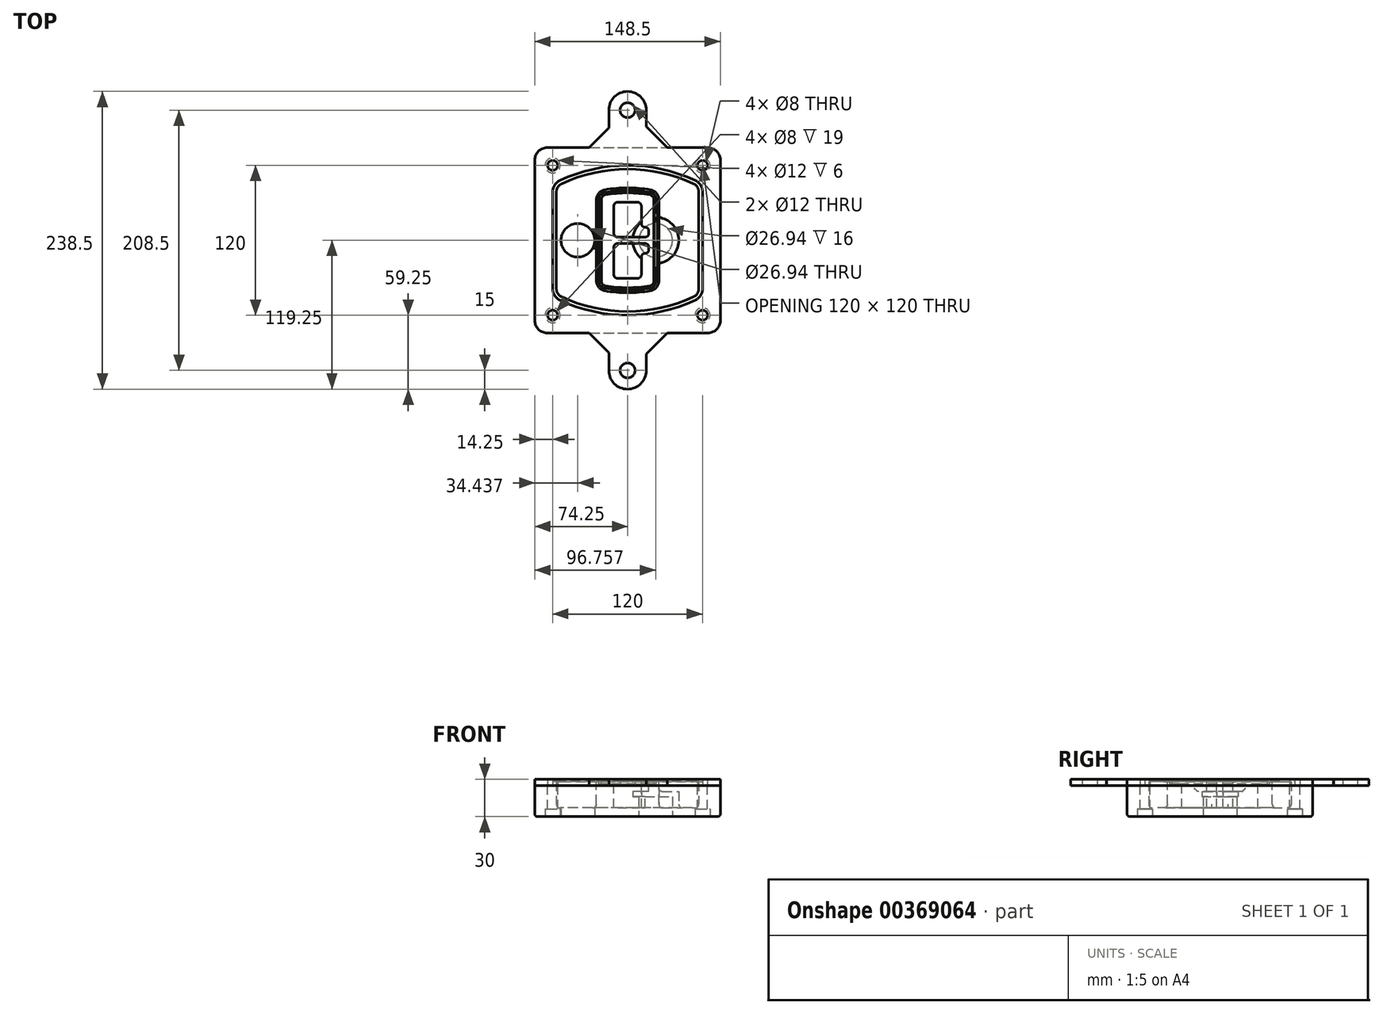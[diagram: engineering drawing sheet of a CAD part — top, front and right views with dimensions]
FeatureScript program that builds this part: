
annotation { "Feature Type Name" : "Feature", "Feature Type Description" : "" }
export const myFeature = defineFeature(function(context is Context, id is Id, definition is map)
    precondition{}
    {
        {
            var Q0;
            Q0=qCreatedBy(makeId("Top.planeOp"),FACE);
            var sketch = newSketch(context, id + "F0", { "sketchPlane" : qUnion([Q0])});
            skPoint(sketch, "E0.rect.middle", {"position": v(0, 0) * mm});
            skLineSegment(sketch, "E1.bottom", {"start": v(-64.25, -74.25) * mm, "end": v(64.25, -74.25) * mm});
            skLineSegment(sketch, "E1.top", {"start": v(-64.25, 74.25) * mm, "end": v(64.25, 74.25) * mm});
            skLineSegment(sketch, "E1.left", {"start": v(-74.25, -64.25) * mm, "end": v(-74.25, 64.25) * mm});
            skLineSegment(sketch, "E1.right", {"start": v(74.25, -64.25) * mm, "end": v(74.25, 64.25) * mm});
            skLineSegment(sketch, "E2", {"start": v(-74.25, 74.25) * mm, "end": v(74.25, -74.25) * mm, "construction": true});
            skLineSegment(sketch, "E3", {"start": v(74.25, 74.25) * mm, "end": v(-74.25, -74.25) * mm, "construction": true});
            skCircle(sketch, "E4", {"center": v(-60, 60) * mm, "radius": 4 * mm});
            skCircle(sketch, "E5", {"center": v(60, 60) * mm, "radius": 4 * mm});
            skCircle(sketch, "E6", {"center": v(60, -60) * mm, "radius": 4 * mm});
            skCircle(sketch, "E7", {"center": v(-60, -60) * mm, "radius": 4 * mm});
            skLineSegment(sketch, "E8", {"start": v(-60, 60) * mm, "end": v(60, 60) * mm, "construction": true});
            skLineSegment(sketch, "E9", {"start": v(60, 60) * mm, "end": v(60, -60) * mm, "construction": true});
            skLineSegment(sketch, "E10", {"start": v(60, -60) * mm, "end": v(-60, -60) * mm, "construction": true});
            skLineSegment(sketch, "E11", {"start": v(-60, -60) * mm, "end": v(-60, 60) * mm, "construction": true});
            skLineSegment(sketch, "E12", {"start": v(-60, 38.83) * mm, "end": v(-60, -38.83) * mm});
            skLineSegment(sketch, "E13", {"start": v(60, 38.83) * mm, "end": v(60, -38.83) * mm});
            skArc(sketch, "E14", {"start": v(54.26, 47.88) * mm, "mid": v(0, 60) * mm, "end": v(-54.26, 47.88) * mm});
            skArc(sketch, "E15", {"start": v(-54.26, -47.88) * mm, "mid": v(0, -60) * mm, "end": v(54.26, -47.88) * mm});
            skLineSegment(sketch, "E16", {"start": v(-60, 0) * mm, "end": v(60, 0) * mm, "construction": true});
            skPoint(sketch, "E17.visualSharp", {"position": v(-60, -45) * mm});
            skArc(sketch, "E17.filletArc", {"start": v(-60, -38.83) * mm, "mid": v(-58.44, -44.2) * mm, "end": v(-54.26, -47.88) * mm});
            skPoint(sketch, "E18.visualSharp", {"position": v(-60, 45) * mm});
            skArc(sketch, "E18.filletArc", {"start": v(-54.26, 47.88) * mm, "mid": v(-58.44, 44.2) * mm, "end": v(-60, 38.83) * mm});
            skPoint(sketch, "E19.visualSharp", {"position": v(60, 45) * mm});
            skArc(sketch, "E19.filletArc", {"start": v(60, 38.83) * mm, "mid": v(58.44, 44.2) * mm, "end": v(54.26, 47.88) * mm});
            skPoint(sketch, "E20.visualSharp", {"position": v(60, -45) * mm});
            skArc(sketch, "E20.filletArc", {"start": v(54.26, -47.88) * mm, "mid": v(58.44, -44.2) * mm, "end": v(60, -38.83) * mm});
            skPoint(sketch, "E21.visualSharp", {"position": v(-74.25, 74.25) * mm});
            skArc(sketch, "E21.filletArc", {"start": v(-64.25, 74.25) * mm, "mid": v(-71.32, 71.32) * mm, "end": v(-74.25, 64.25) * mm});
            skPoint(sketch, "E22.visualSharp", {"position": v(74.25, 74.25) * mm});
            skArc(sketch, "E22.filletArc", {"start": v(74.25, 64.25) * mm, "mid": v(71.32, 71.32) * mm, "end": v(64.25, 74.25) * mm});
            skPoint(sketch, "E23.visualSharp", {"position": v(74.25, -74.25) * mm});
            skArc(sketch, "E23.filletArc", {"start": v(64.25, -74.25) * mm, "mid": v(71.32, -71.32) * mm, "end": v(74.25, -64.25) * mm});
            skPoint(sketch, "E24.visualSharp", {"position": v(-74.25, -74.25) * mm});
            skArc(sketch, "E24.filletArc", {"start": v(-74.25, -64.25) * mm, "mid": v(-71.32, -71.32) * mm, "end": v(-64.25, -74.25) * mm});
            skArc(sketch, "E25.0", {"start": v(57, 38.83) * mm, "mid": v(55.9, 42.58) * mm, "end": v(52.98, 45.17) * mm});
            skLineSegment(sketch, "E25.1", {"start": v(57, 38.83) * mm, "end": v(57, -38.83) * mm});
            skArc(sketch, "E25.2", {"start": v(52.98, -45.17) * mm, "mid": v(55.9, -42.58) * mm, "end": v(57, -38.83) * mm});
            skArc(sketch, "E25.3", {"start": v(-52.98, -45.17) * mm, "mid": v(0, -57) * mm, "end": v(52.98, -45.17) * mm});
            skArc(sketch, "E25.4", {"start": v(-57, -38.83) * mm, "mid": v(-55.9, -42.58) * mm, "end": v(-52.98, -45.17) * mm});
            skArc(sketch, "E25.5", {"start": v(52.98, 45.17) * mm, "mid": v(0, 57) * mm, "end": v(-52.98, 45.17) * mm});
            skLineSegment(sketch, "E25.6", {"start": v(-57, 38.83) * mm, "end": v(-57, -38.83) * mm});
            skArc(sketch, "E25.7", {"start": v(-52.98, 45.17) * mm, "mid": v(-55.9, 42.58) * mm, "end": v(-57, 38.83) * mm});
            skArc(sketch, "E26.0", {"start": v(-55.96, 51.5) * mm, "mid": v(-61.82, 46.33) * mm, "end": v(-64, 38.83) * mm});
            skArc(sketch, "E26.1", {"start": v(55.96, 51.5) * mm, "mid": v(0, 64) * mm, "end": v(-55.96, 51.5) * mm});
            skArc(sketch, "E26.2", {"start": v(64, 38.83) * mm, "mid": v(61.82, 46.33) * mm, "end": v(55.96, 51.5) * mm});
            skLineSegment(sketch, "E26.3", {"start": v(64, 38.83) * mm, "end": v(64, -38.83) * mm});
            skArc(sketch, "E26.4", {"start": v(55.96, -51.5) * mm, "mid": v(61.82, -46.33) * mm, "end": v(64, -38.83) * mm});
            skLineSegment(sketch, "E26.5", {"start": v(-64, 38.83) * mm, "end": v(-64, -38.83) * mm});
            skArc(sketch, "E26.6", {"start": v(-55.96, -51.5) * mm, "mid": v(0, -64) * mm, "end": v(55.96, -51.5) * mm});
            skArc(sketch, "E26.7", {"start": v(-64, -38.83) * mm, "mid": v(-61.82, -46.33) * mm, "end": v(-55.96, -51.5) * mm});
            skSolve(sketch);
        }
        {
            var Q0;
            Q0=makeQuery(id+"F0.imprint","IMPRINT",FACE,{"disambiguationData":[TD([[makeQuery(id+"F0.imprint","IMPRINT",EDGE,{"derivedFrom":sQuery(id+"F0.wireOp",EDGE,"E1.bottom")}),1.0]])]});
            var Q1;
            Q1=makeQuery(id+"F0.imprint","IMPRINT",FACE,{"disambiguationData":[TD([[makeQuery(id+"F0.imprint","IMPRINT",EDGE,{"derivedFrom":sQuery(id+"F0.wireOp",EDGE,"E12")}),1.0]])]});
            var Q2;
            Q2=makeQuery(id+"F0.imprint","IMPRINT",FACE,{"disambiguationData":[TD([[makeQuery(id+"F0.imprint","IMPRINT",EDGE,{"derivedFrom":sQuery(id+"F0.wireOp",EDGE,"E25.0")}),1.0]])]});
            var Q3;
            Q3=makeQuery(id+"F0.imprint","IMPRINT",FACE,{"disambiguationData":[TD([[makeQuery(id+"F0.imprint","IMPRINT",EDGE,{"derivedFrom":sQuery(id+"F0.wireOp",EDGE,"E12")}),-1.0]])]});
            extrude(context, id + "F1", {"entities" : qUnion([Q0, Q1, Q2, Q3]), "oppositeDirection" : true, "depth" : 25 * mm});
        }
        {
            var Q0;
            Q0=makeQuery(id+"F0.imprint","IMPRINT",FACE,{"disambiguationData":[TD([[makeQuery(id+"F0.imprint","IMPRINT",EDGE,{"derivedFrom":sQuery(id+"F0.wireOp",EDGE,"E12")}),1.0]])]});
            extrude(context, id + "F2", {"entities" : qUnion([Q0]), "operationType" : NewBodyOperationType.ADD, "depth" : 3 * mm});
        }
        {
            var Q0;
            Q0=makeQuery(id+"F0.imprint","IMPRINT",FACE,{"disambiguationData":[TD([[makeQuery(id+"F0.imprint","IMPRINT",EDGE,{"derivedFrom":sQuery(id+"F0.wireOp",EDGE,"E25.0")}),1.0]])]});
            extrude(context, id + "F3", {"entities" : qUnion([Q0]), "operationType" : NewBodyOperationType.REMOVE, "oppositeDirection" : true, "depth" : 18 * mm});
        }
        {
            var Q0;
            Q0=makeQuery(id+"F2.opExtrude","CAP_FACE",FACE,{"disambiguationData":[OSD([sQuery(id+"F0.wireOp",EDGE,"E12"),sQuery(id+"F0.wireOp",EDGE,"E13"),sQuery(id+"F0.wireOp",EDGE,"E14"),sQuery(id+"F0.wireOp",EDGE,"E15"),sQuery(id+"F0.wireOp",EDGE,"E17.filletArc"),sQuery(id+"F0.wireOp",EDGE,"E18.filletArc"),sQuery(id+"F0.wireOp",EDGE,"E19.filletArc"),sQuery(id+"F0.wireOp",EDGE,"E20.filletArc"),sQuery(id+"F0.wireOp",EDGE,"E25.0"),sQuery(id+"F0.wireOp",EDGE,"E25.1"),sQuery(id+"F0.wireOp",EDGE,"E25.2"),sQuery(id+"F0.wireOp",EDGE,"E25.3"),sQuery(id+"F0.wireOp",EDGE,"E25.4"),sQuery(id+"F0.wireOp",EDGE,"E25.5"),sQuery(id+"F0.wireOp",EDGE,"E25.6"),sQuery(id+"F0.wireOp",EDGE,"E25.7")])],"isStart":false});
            var sketch = newSketch(context, id + "F4", { "sketchPlane" : qUnion([Q0])});
            skArc(sketch, "E27.0", {"start": v(-18.34, -40.45) * mm, "mid": v(0, -42) * mm, "end": v(18.34, -40.45) * mm});
            skArc(sketch, "E28.0", {"start": v(18.34, 40.45) * mm, "mid": v(0, 42) * mm, "end": v(-18.34, 40.45) * mm});
            skLineSegment(sketch, "E29", {"start": v(-25, 32.57) * mm, "end": v(-25, -32.57) * mm});
            skLineSegment(sketch, "E30", {"start": v(25, 32.57) * mm, "end": v(25, -32.57) * mm});
            skLineSegment(sketch, "E31", {"start": v(-25, 39.1) * mm, "end": v(25, 39.1) * mm, "construction": true});
            skLineSegment(sketch, "E32", {"start": v(-25, -39.1) * mm, "end": v(25, -39.1) * mm, "construction": true});
            skPoint(sketch, "E33.visualSharp", {"position": v(-25, 39.1) * mm});
            skArc(sketch, "E33.filletArc", {"start": v(-18.34, 40.45) * mm, "mid": v(-23.11, 37.73) * mm, "end": v(-25, 32.57) * mm});
            skPoint(sketch, "E34.visualSharp", {"position": v(25, 39.1) * mm});
            skArc(sketch, "E34.filletArc", {"start": v(25, 32.57) * mm, "mid": v(23.11, 37.73) * mm, "end": v(18.34, 40.45) * mm});
            skPoint(sketch, "E35.visualSharp", {"position": v(25, -39.1) * mm});
            skArc(sketch, "E35.filletArc", {"start": v(18.34, -40.45) * mm, "mid": v(23.11, -37.73) * mm, "end": v(25, -32.57) * mm});
            skPoint(sketch, "E36.visualSharp", {"position": v(-25, -39.1) * mm});
            skArc(sketch, "E36.filletArc", {"start": v(-25, -32.57) * mm, "mid": v(-23.11, -37.73) * mm, "end": v(-18.34, -40.45) * mm});
            skArc(sketch, "E37.0", {"start": v(52.98, 45.17) * mm, "mid": v(0, 57) * mm, "end": v(-52.98, 45.17) * mm});
            skArc(sketch, "E37.1", {"start": v(-52.98, 45.17) * mm, "mid": v(-55.9, 42.58) * mm, "end": v(-57, 38.83) * mm});
            skLineSegment(sketch, "E37.2", {"start": v(-57, 38.83) * mm, "end": v(-57, -38.83) * mm});
            skArc(sketch, "E37.3", {"start": v(-57, -38.83) * mm, "mid": v(-55.9, -42.58) * mm, "end": v(-52.98, -45.17) * mm});
            skArc(sketch, "E37.4", {"start": v(-52.98, -45.17) * mm, "mid": v(0, -57) * mm, "end": v(52.98, -45.17) * mm});
            skArc(sketch, "E37.5", {"start": v(52.98, -45.17) * mm, "mid": v(55.9, -42.58) * mm, "end": v(57, -38.83) * mm});
            skLineSegment(sketch, "E37.6", {"start": v(57, 38.83) * mm, "end": v(57, -38.83) * mm});
            skArc(sketch, "E37.7", {"start": v(57, 38.83) * mm, "mid": v(55.9, 42.58) * mm, "end": v(52.98, 45.17) * mm});
            skLineSegment(sketch, "E38.0", {"start": v(23, 32.57) * mm, "end": v(23, -32.57) * mm});
            skArc(sketch, "E38.1", {"start": v(18, -38.48) * mm, "mid": v(21.58, -36.44) * mm, "end": v(23, -32.57) * mm});
            skArc(sketch, "E38.2", {"start": v(-18, -38.48) * mm, "mid": v(0, -40) * mm, "end": v(18, -38.48) * mm});
            skArc(sketch, "E38.3", {"start": v(-23, -32.57) * mm, "mid": v(-21.58, -36.44) * mm, "end": v(-18, -38.48) * mm});
            skLineSegment(sketch, "E38.4", {"start": v(-23, 32.57) * mm, "end": v(-23, -32.57) * mm});
            skArc(sketch, "E38.5", {"start": v(23, 32.57) * mm, "mid": v(21.58, 36.44) * mm, "end": v(18, 38.48) * mm});
            skArc(sketch, "E38.6", {"start": v(-18, 38.48) * mm, "mid": v(-21.58, 36.44) * mm, "end": v(-23, 32.57) * mm});
            skArc(sketch, "E38.7", {"start": v(18, 38.48) * mm, "mid": v(0, 40) * mm, "end": v(-18, 38.48) * mm});
            skArc(sketch, "E39.0", {"start": v(21, 32.57) * mm, "mid": v(20.06, 35.15) * mm, "end": v(17.67, 36.5) * mm});
            skLineSegment(sketch, "E39.1", {"start": v(21, 32.57) * mm, "end": v(21, -32.57) * mm});
            skArc(sketch, "E39.2", {"start": v(17.67, -36.5) * mm, "mid": v(20.06, -35.15) * mm, "end": v(21, -32.57) * mm});
            skArc(sketch, "E39.3", {"start": v(-17.67, -36.5) * mm, "mid": v(0, -38) * mm, "end": v(17.67, -36.5) * mm});
            skArc(sketch, "E39.4", {"start": v(-21, -32.57) * mm, "mid": v(-20.06, -35.15) * mm, "end": v(-17.67, -36.5) * mm});
            skArc(sketch, "E39.5", {"start": v(17.67, 36.5) * mm, "mid": v(0, 38) * mm, "end": v(-17.67, 36.5) * mm});
            skLineSegment(sketch, "E39.6", {"start": v(-21, 32.57) * mm, "end": v(-21, -32.57) * mm});
            skArc(sketch, "E39.7", {"start": v(-17.67, 36.5) * mm, "mid": v(-20.06, 35.15) * mm, "end": v(-21, 32.57) * mm});
            skLineSegment(sketch, "E40", {"start": v(-25, 0) * mm, "end": v(25, 0) * mm, "construction": true});
            skLineSegment(sketch, "E41", {"start": v(-11, 5.5) * mm, "end": v(-11, 27.5) * mm});
            skLineSegment(sketch, "E42", {"start": v(-8, 30.5) * mm, "end": v(8, 30.5) * mm});
            skLineSegment(sketch, "E43", {"start": v(11, 27.5) * mm, "end": v(11, 13.5) * mm});
            skLineSegment(sketch, "E44", {"start": v(14, 10.5) * mm, "end": v(14, 10.5) * mm});
            skLineSegment(sketch, "E45", {"start": v(17, 7.5) * mm, "end": v(17, 5.5) * mm});
            skLineSegment(sketch, "E46", {"start": v(14, 2.5) * mm, "end": v(-8, 2.5) * mm});
            skPoint(sketch, "E47.visualSharp", {"position": v(-11, 30.5) * mm});
            skArc(sketch, "E47.filletArc", {"start": v(-8, 30.5) * mm, "mid": v(-10.12, 29.62) * mm, "end": v(-11, 27.5) * mm});
            skPoint(sketch, "E48.visualSharp", {"position": v(11, 30.5) * mm});
            skArc(sketch, "E48.filletArc", {"start": v(11, 27.5) * mm, "mid": v(10.12, 29.62) * mm, "end": v(8, 30.5) * mm});
            skPoint(sketch, "E49.visualSharp", {"position": v(11, 10.5) * mm});
            skArc(sketch, "E49.filletArc", {"start": v(11, 13.5) * mm, "mid": v(11.88, 11.38) * mm, "end": v(14, 10.5) * mm});
            skPoint(sketch, "E50.visualSharp", {"position": v(17, 10.5) * mm});
            skArc(sketch, "E50.filletArc", {"start": v(17, 7.5) * mm, "mid": v(16.12, 9.62) * mm, "end": v(14, 10.5) * mm});
            skPoint(sketch, "E51.visualSharp", {"position": v(17, 2.5) * mm});
            skArc(sketch, "E51.filletArc", {"start": v(14, 2.5) * mm, "mid": v(16.12, 3.38) * mm, "end": v(17, 5.5) * mm});
            skPoint(sketch, "E52.visualSharp", {"position": v(-11, 2.5) * mm});
            skArc(sketch, "E52.filletArc", {"start": v(-11, 5.5) * mm, "mid": v(-10.12, 3.38) * mm, "end": v(-8, 2.5) * mm});
            skLineSegment(sketch, "E53.0.MirrorCS", {"start": v(14, -2.5) * mm, "end": v(-8, -2.5) * mm});
            skArc(sketch, "E54.0.MirrorCS", {"start": v(-11, -5.5) * mm, "mid": v(-10.12, -3.38) * mm, "end": v(-8, -2.5) * mm});
            skLineSegment(sketch, "E55.0.MirrorCS", {"start": v(-11, -5.5) * mm, "end": v(-11, -27.5) * mm});
            skArc(sketch, "E56.0.MirrorCS", {"start": v(-8, -30.5) * mm, "mid": v(-10.12, -29.62) * mm, "end": v(-11, -27.5) * mm});
            skLineSegment(sketch, "E57.0.MirrorCS", {"start": v(-8, -30.5) * mm, "end": v(8, -30.5) * mm});
            skArc(sketch, "E58.0.MirrorCS", {"start": v(11, -27.5) * mm, "mid": v(10.12, -29.62) * mm, "end": v(8, -30.5) * mm});
            skLineSegment(sketch, "E59.0.MirrorCS", {"start": v(11, -27.5) * mm, "end": v(11, -13.5) * mm});
            skArc(sketch, "E60.0.MirrorCS", {"start": v(11, -13.5) * mm, "mid": v(11.88, -11.38) * mm, "end": v(14, -10.5) * mm});
            skArc(sketch, "E61.0.MirrorCS", {"start": v(17, -7.5) * mm, "mid": v(16.12, -9.62) * mm, "end": v(14, -10.5) * mm});
            skLineSegment(sketch, "E62.0.MirrorCS", {"start": v(17, -7.5) * mm, "end": v(17, -5.5) * mm});
            skArc(sketch, "E63.0.MirrorCS", {"start": v(14, -2.5) * mm, "mid": v(16.12, -3.38) * mm, "end": v(17, -5.5) * mm});
            skSolve(sketch);
        }
        {
            var Q0;
            Q0=makeQuery(id+"F4.imprint","IMPRINT",FACE,{"disambiguationData":[TD([[makeQuery(id+"F4.imprint","IMPRINT",EDGE,{"derivedFrom":sQuery(id+"F4.wireOp",EDGE,"E27.0")}),1.0]])]});
            var Q1;
            Q1=makeQuery(id+"F4.imprint","IMPRINT",FACE,{"disambiguationData":[TD([[makeQuery(id+"F4.imprint","IMPRINT",EDGE,{"derivedFrom":sQuery(id+"F4.wireOp",EDGE,"E38.0")}),-1.0]])]});
            var Q2;
            Q2=makeQuery(id+"F4.imprint","IMPRINT",FACE,{"disambiguationData":[TD([[makeQuery(id+"F4.imprint","IMPRINT",EDGE,{"derivedFrom":sQuery(id+"F4.wireOp",EDGE,"E39.0")}),1.0]])]});
            extrude(context, id + "F5", {"entities" : qUnion([Q0, Q1, Q2]), "operationType" : NewBodyOperationType.ADD, "endBound" : BoundingType.UP_TO_NEXT, "oppositeDirection" : true, "depth" : 25 * mm});
        }
        {
            var Q0;
            Q0=makeQuery(id+"F4.imprint","IMPRINT",FACE,{"disambiguationData":[TD([[makeQuery(id+"F4.imprint","IMPRINT",EDGE,{"derivedFrom":sQuery(id+"F4.wireOp",EDGE,"E38.0")}),-1.0]])]});
            extrude(context, id + "F6", {"entities" : qUnion([Q0]), "operationType" : NewBodyOperationType.REMOVE, "oppositeDirection" : true, "depth" : 2 * mm});
        }
        {
            var Q0;
            Q0=makeQuery(id+"F1.opExtrude","CAP_FACE",FACE,{"disambiguationData":[OSD([sQuery(id+"F0.wireOp",EDGE,"E1.bottom"),sQuery(id+"F0.wireOp",EDGE,"E1.top"),sQuery(id+"F0.wireOp",EDGE,"E1.left"),sQuery(id+"F0.wireOp",EDGE,"E1.right"),sQuery(id+"F0.wireOp",EDGE,"E4"),sQuery(id+"F0.wireOp",EDGE,"E5"),sQuery(id+"F0.wireOp",EDGE,"E6"),sQuery(id+"F0.wireOp",EDGE,"E7"),sQuery(id+"F0.wireOp",EDGE,"E21.filletArc"),sQuery(id+"F0.wireOp",EDGE,"E22.filletArc"),sQuery(id+"F0.wireOp",EDGE,"E23.filletArc"),sQuery(id+"F0.wireOp",EDGE,"E24.filletArc")])],"isStart":false});
            var sketch = newSketch(context, id + "F7", { "sketchPlane" : qUnion([Q0])});
            skCircle(sketch, "E64", {"center": v(22.5, 0) * mm, "radius": 13.47 * mm});
            skCircle(sketch, "E65", {"center": v(-39.81, 0) * mm, "radius": 13.47 * mm});
            skLineSegment(sketch, "E66", {"start": v(74.25, 0) * mm, "end": v(-74.25, 0) * mm});
            skCircle(sketch, "E67", {"center": v(22.5, 0) * mm, "radius": 18.47 * mm});
            skCircle(sketch, "E68", {"center": v(60, -60) * mm, "radius": 6 * mm});
            skCircle(sketch, "E69", {"center": v(-60, -60) * mm, "radius": 6 * mm});
            skCircle(sketch, "E70", {"center": v(-60, 60) * mm, "radius": 6 * mm});
            skCircle(sketch, "E71", {"center": v(60, 60) * mm, "radius": 6 * mm});
            skSolve(sketch);
        }
        {
            var Q0;
            {var subQ1=sQuery(id+"F7.wireOp",EDGE,"E66");var subQ4=sQuery(id+"F7.wireOp",EDGE,"E64");var subQ6=makeQuery(id+"F7.imprint","INTERSECT",VERTEX,{"disambiguationData":[OD(0.0)],"derivedFrom":[subQ4,subQ1]});Q0=makeQuery(id+"F7.imprint","IMPRINT",FACE,{"disambiguationData":[TD([[makeQuery(id+"F7.imprint","IMPRINT",EDGE,{"disambiguationData":[TD([[subQ6,-1.0]])],"derivedFrom":subQ4}),-1.0]])]});}
            var Q1;
            {var subQ0=sQuery(id+"F7.wireOp",EDGE,"E66");var subQ1=sQuery(id+"F7.wireOp",EDGE,"E64");var subQ3=makeQuery(id+"F7.imprint","INTERSECT",VERTEX,{"disambiguationData":[OD(0.0)],"derivedFrom":[subQ1,subQ0]});Q1=makeQuery(id+"F7.imprint","IMPRINT",FACE,{"disambiguationData":[TD([[makeQuery(id+"F7.imprint","IMPRINT",EDGE,{"disambiguationData":[TD([[subQ3,-1.0]])],"derivedFrom":subQ1}),1.0]])]});}
            var Q2;
            {var subQ0=sQuery(id+"F7.wireOp",EDGE,"E66");var subQ1=sQuery(id+"F7.wireOp",EDGE,"E64");var subQ3=makeQuery(id+"F7.imprint","INTERSECT",VERTEX,{"disambiguationData":[OD(0.0)],"derivedFrom":[subQ1,subQ0]});Q2=makeQuery(id+"F7.imprint","IMPRINT",FACE,{"disambiguationData":[TD([[makeQuery(id+"F7.imprint","IMPRINT",EDGE,{"disambiguationData":[TD([[subQ3,1.0]])],"derivedFrom":subQ1}),1.0]])]});}
            var Q3;
            {var subQ1=sQuery(id+"F7.wireOp",EDGE,"E66");var subQ4=sQuery(id+"F7.wireOp",EDGE,"E64");var subQ6=makeQuery(id+"F7.imprint","INTERSECT",VERTEX,{"disambiguationData":[OD(0.0)],"derivedFrom":[subQ4,subQ1]});Q3=makeQuery(id+"F7.imprint","IMPRINT",FACE,{"disambiguationData":[TD([[makeQuery(id+"F7.imprint","IMPRINT",EDGE,{"disambiguationData":[TD([[subQ6,1.0]])],"derivedFrom":subQ4}),-1.0]])]});}
            extrude(context, id + "F8", {"entities" : qUnion([Q0, Q1, Q2, Q3]), "operationType" : NewBodyOperationType.ADD, "oppositeDirection" : true, "depth" : 20 * mm});
        }
        {
            var Q0;
            {var subQ0=sQuery(id+"F7.wireOp",EDGE,"E66");var subQ1=sQuery(id+"F7.wireOp",EDGE,"E64");var subQ3=makeQuery(id+"F7.imprint","INTERSECT",VERTEX,{"disambiguationData":[OD(0.0)],"derivedFrom":[subQ1,subQ0]});Q0=makeQuery(id+"F7.imprint","IMPRINT",FACE,{"disambiguationData":[TD([[makeQuery(id+"F7.imprint","IMPRINT",EDGE,{"disambiguationData":[TD([[subQ3,-1.0]])],"derivedFrom":subQ1}),1.0]])]});}
            var Q1;
            {var subQ0=sQuery(id+"F7.wireOp",EDGE,"E66");var subQ1=sQuery(id+"F7.wireOp",EDGE,"E64");var subQ3=makeQuery(id+"F7.imprint","INTERSECT",VERTEX,{"disambiguationData":[OD(0.0)],"derivedFrom":[subQ1,subQ0]});Q1=makeQuery(id+"F7.imprint","IMPRINT",FACE,{"disambiguationData":[TD([[makeQuery(id+"F7.imprint","IMPRINT",EDGE,{"disambiguationData":[TD([[subQ3,1.0]])],"derivedFrom":subQ1}),1.0]])]});}
            extrude(context, id + "F9", {"entities" : qUnion([Q0, Q1]), "operationType" : NewBodyOperationType.REMOVE, "oppositeDirection" : true, "depth" : 16 * mm});
        }
        {
            var Q0;
            {var subQ0=sQuery(id+"F7.wireOp",EDGE,"E66");var subQ1=sQuery(id+"F7.wireOp",EDGE,"E65");var subQ3=makeQuery(id+"F7.imprint","INTERSECT",VERTEX,{"disambiguationData":[OD(0.0)],"derivedFrom":[subQ1,subQ0]});Q0=makeQuery(id+"F7.imprint","IMPRINT",FACE,{"disambiguationData":[TD([[makeQuery(id+"F7.imprint","IMPRINT",EDGE,{"disambiguationData":[TD([[subQ3,-1.0]])],"derivedFrom":subQ1}),1.0]])]});}
            var Q1;
            {var subQ0=sQuery(id+"F7.wireOp",EDGE,"E66");var subQ1=sQuery(id+"F7.wireOp",EDGE,"E65");var subQ3=makeQuery(id+"F7.imprint","INTERSECT",VERTEX,{"disambiguationData":[OD(0.0)],"derivedFrom":[subQ1,subQ0]});Q1=makeQuery(id+"F7.imprint","IMPRINT",FACE,{"disambiguationData":[TD([[makeQuery(id+"F7.imprint","IMPRINT",EDGE,{"disambiguationData":[TD([[subQ3,1.0]])],"derivedFrom":subQ1}),1.0]])]});}
            extrude(context, id + "F10", {"entities" : qUnion([Q0, Q1]), "operationType" : NewBodyOperationType.REMOVE, "oppositeDirection" : true, "depth" : 25 * mm});
        }
        {
            var Q0;
            Q0=makeQuery(id+"F7.imprint","IMPRINT",FACE,{"disambiguationData":[TD([[makeQuery(id+"F7.imprint","IMPRINT",EDGE,{"derivedFrom":sQuery(id+"F7.wireOp",EDGE,"E68")}),1.0]])]});
            var Q1;
            Q1=makeQuery(id+"F7.imprint","IMPRINT",FACE,{"disambiguationData":[TD([[makeQuery(id+"F7.imprint","IMPRINT",EDGE,{"derivedFrom":makeQuery(id+"F1.opExtrude","CAP_EDGE",EDGE,{"disambiguationData":[OSD([sQuery(id+"F0.wireOp",EDGE,"E5")])],"isStart":false})}),-1.0]])]});
            var Q2;
            Q2=makeQuery(id+"F7.imprint","IMPRINT",FACE,{"disambiguationData":[TD([[makeQuery(id+"F7.imprint","IMPRINT",EDGE,{"derivedFrom":sQuery(id+"F7.wireOp",EDGE,"E69")}),1.0]])]});
            var Q3;
            Q3=makeQuery(id+"F7.imprint","IMPRINT",FACE,{"disambiguationData":[TD([[makeQuery(id+"F7.imprint","IMPRINT",EDGE,{"derivedFrom":makeQuery(id+"F1.opExtrude","CAP_EDGE",EDGE,{"disambiguationData":[OSD([sQuery(id+"F0.wireOp",EDGE,"E4")])],"isStart":false})}),-1.0]])]});
            var Q4;
            Q4=makeQuery(id+"F7.imprint","IMPRINT",FACE,{"disambiguationData":[TD([[makeQuery(id+"F7.imprint","IMPRINT",EDGE,{"derivedFrom":sQuery(id+"F7.wireOp",EDGE,"E70")}),1.0]])]});
            var Q5;
            Q5=makeQuery(id+"F7.imprint","IMPRINT",FACE,{"disambiguationData":[TD([[makeQuery(id+"F7.imprint","IMPRINT",EDGE,{"derivedFrom":makeQuery(id+"F1.opExtrude","CAP_EDGE",EDGE,{"disambiguationData":[OSD([sQuery(id+"F0.wireOp",EDGE,"E7")])],"isStart":false})}),-1.0]])]});
            var Q6;
            Q6=makeQuery(id+"F7.imprint","IMPRINT",FACE,{"disambiguationData":[TD([[makeQuery(id+"F7.imprint","IMPRINT",EDGE,{"derivedFrom":sQuery(id+"F7.wireOp",EDGE,"E71")}),1.0]])]});
            var Q7;
            Q7=makeQuery(id+"F7.imprint","IMPRINT",FACE,{"disambiguationData":[TD([[makeQuery(id+"F7.imprint","IMPRINT",EDGE,{"derivedFrom":makeQuery(id+"F1.opExtrude","CAP_EDGE",EDGE,{"disambiguationData":[OSD([sQuery(id+"F0.wireOp",EDGE,"E6")])],"isStart":false})}),-1.0]])]});
            extrude(context, id + "F11", {"entities" : qUnion([Q0, Q1, Q2, Q3, Q4, Q5, Q6, Q7]), "operationType" : NewBodyOperationType.REMOVE, "oppositeDirection" : true, "depth" : 6 * mm});
        }
        {
            var Q0;
            Q0=makeQuery(id+"F9.boolean.opBoolean","COPY",FACE,{"derivedFrom":makeQuery(id+"F9.opExtrude","CAP_FACE",FACE,{"disambiguationData":[OSD([sQuery(id+"F7.wireOp",EDGE,"E64")])],"isStart":false})});
            var sketch = newSketch(context, id + "F12", { "sketchPlane" : qUnion([Q0])});
            skArc(sketch, "E72.0", {"start": v(11, 14.45) * mm, "mid": v(6.45, 9.13) * mm, "end": v(4.2, 2.5) * mm});
            skArc(sketch, "E72.1", {"start": v(4.2, -2.5) * mm, "mid": v(6.45, -9.13) * mm, "end": v(11, -14.45) * mm});
            skLineSegment(sketch, "E73", {"start": v(4.2, -2.5) * mm, "end": v(14, -2.5) * mm});
            skLineSegment(sketch, "E74.0", {"start": v(14, 2.5) * mm, "end": v(4.2, 2.5) * mm});
            skArc(sketch, "E74.1", {"start": v(14, 2.5) * mm, "mid": v(16.12, 3.38) * mm, "end": v(17, 5.5) * mm});
            skLineSegment(sketch, "E74.2", {"start": v(17, 7.5) * mm, "end": v(17, 5.5) * mm});
            skArc(sketch, "E74.3", {"start": v(17, 7.5) * mm, "mid": v(16.12, 9.62) * mm, "end": v(14, 10.5) * mm});
            skArc(sketch, "E74.4", {"start": v(11, 13.5) * mm, "mid": v(11.88, 11.38) * mm, "end": v(14, 10.5) * mm});
            skLineSegment(sketch, "E74.5", {"start": v(11, 14.45) * mm, "end": v(11, 13.5) * mm});
            skLineSegment(sketch, "E74.7", {"start": v(14, -2.5) * mm, "end": v(4.2, -2.5) * mm});
            skArc(sketch, "E74.8", {"start": v(14, -2.5) * mm, "mid": v(16.12, -3.38) * mm, "end": v(17, -5.5) * mm});
            skLineSegment(sketch, "E74.9", {"start": v(17, -7.5) * mm, "end": v(17, -5.5) * mm});
            skArc(sketch, "E74.10", {"start": v(17, -7.5) * mm, "mid": v(16.12, -9.62) * mm, "end": v(14, -10.5) * mm});
            skArc(sketch, "E74.11", {"start": v(11, -13.5) * mm, "mid": v(11.88, -11.38) * mm, "end": v(14, -10.5) * mm});
            skLineSegment(sketch, "E74.12", {"start": v(11, -14.45) * mm, "end": v(11, -13.5) * mm});
            skPoint(sketch, "E75.orphan", {"position": v(11, -27.5) * mm});
            skPoint(sketch, "E76.orphan", {"position": v(-8, -2.5) * mm});
            skPoint(sketch, "E77.orphan", {"position": v(-8, 2.5) * mm});
            skPoint(sketch, "E78.orphan", {"position": v(11, 27.5) * mm});
            skSolve(sketch);
        }
        {
            var Q0;
            {var subQ7=sQuery(id+"F12.wireOp",EDGE,"E72.0");var subQ14=sQuery(id+"F12.wireOp",EDGE,"E72.1");var subQ16=sQuery(id+"F12.wireOp",EDGE,"E74.1");var subQ18=sQuery(id+"F12.wireOp",EDGE,"E74.8");Q0=qUnion([makeQuery(id+"F12.imprint","IMPRINT",FACE,{"disambiguationData":[TD([[makeQuery(id+"F12.imprint","IMPRINT",EDGE,{"derivedFrom":subQ7}),1.0]])]}),makeQuery(id+"F12.imprint","IMPRINT",FACE,{"disambiguationData":[TD([[makeQuery(id+"F12.imprint","IMPRINT",EDGE,{"derivedFrom":subQ14}),1.0]])]}),makeQuery(id+"F12.imprint","IMPRINT",FACE,{"disambiguationData":[TD([[makeQuery(id+"F12.imprint","IMPRINT",EDGE,{"derivedFrom":subQ16}),1.0]])]}),makeQuery(id+"F12.imprint","IMPRINT",FACE,{"disambiguationData":[TD([[makeQuery(id+"F12.imprint","IMPRINT",EDGE,{"derivedFrom":subQ18}),-1.0]])]})]);}
            var Q1;
            Q1=makeQuery(id+"F5.boolean.opBoolean","SPLIT",FACE,{"disambiguationData":[TD([makeQuery(id+"F5.opExtrude","SWEPT_FACE",FACE,{"disambiguationData":[OSD([sQuery(id+"F4.wireOp",EDGE,"E41")])]})])],"derivedFrom":makeQuery(id+"F3.boolean.opBoolean","COPY",FACE,{"derivedFrom":makeQuery(id+"F3.opExtrude","CAP_FACE",FACE,{"disambiguationData":[OSD([sQuery(id+"F0.wireOp",EDGE,"E25.0"),sQuery(id+"F0.wireOp",EDGE,"E25.1"),sQuery(id+"F0.wireOp",EDGE,"E25.2"),sQuery(id+"F0.wireOp",EDGE,"E25.3"),sQuery(id+"F0.wireOp",EDGE,"E25.4"),sQuery(id+"F0.wireOp",EDGE,"E25.5"),sQuery(id+"F0.wireOp",EDGE,"E25.6"),sQuery(id+"F0.wireOp",EDGE,"E25.7")])],"isStart":false})})});
            extrude(context, id + "F13", {"entities" : qUnion([Q0]), "operationType" : NewBodyOperationType.REMOVE, "endBound" : BoundingType.UP_TO_SURFACE, "endBoundEntityFace" : qUnion([Q1]), "depth" : 25 * mm});
        }
        {
            var Q0;
            Q0=makeQuery(id+"F3.boolean.opBoolean","COPY",EDGE,{"derivedFrom":makeQuery(id+"F3.opExtrude","CAP_EDGE",EDGE,{"disambiguationData":[OSD([sQuery(id+"F0.wireOp",EDGE,"E25.6")])],"isStart":false})});
            var Q1;
            Q1=makeQuery(id+"F8.boolean.opBoolean","INTERSECT",EDGE,{"derivedFrom":[makeQuery(id+"F5.opExtrude","SWEPT_FACE",FACE,{"disambiguationData":[OSD([sQuery(id+"F4.wireOp",EDGE,"E30")])]}),makeQuery(id+"F8.opExtrude","CAP_FACE",FACE,{"disambiguationData":[OSD([sQuery(id+"F7.wireOp",EDGE,"E67")])],"isStart":false})]});
            var Q2;
            Q2=makeQuery(id+"F8.boolean.opBoolean","INTERSECT",EDGE,{"disambiguationData":[OD(1.0)],"derivedFrom":[makeQuery(id+"F5.opExtrude","SWEPT_FACE",FACE,{"disambiguationData":[OSD([sQuery(id+"F4.wireOp",EDGE,"E30")])]}),makeQuery(id+"F8.opExtrude","SWEPT_FACE",FACE,{"disambiguationData":[OSD([sQuery(id+"F7.wireOp",EDGE,"E67")])]})]});
            var Q3;
            {var subQ0=sQuery(id+"F4.wireOp",EDGE,"E30");Q3=makeQuery(id+"F8.boolean.opBoolean","SPLIT",EDGE,{"disambiguationData":[TD([makeQuery(id+"F5.opExtrude","SWEPT_FACE",FACE,{"disambiguationData":[OSD([sQuery(id+"F4.wireOp",EDGE,"E35.filletArc")])]})])],"derivedFrom":makeQuery(id+"F5.opExtrude","CAP_EDGE",EDGE,{"disambiguationData":[OSD([subQ0])],"isStart":false})});}
            var Q4;
            {var subQ0=sQuery(id+"F0.wireOp",EDGE,"E25.7");var subQ1=sQuery(id+"F0.wireOp",EDGE,"E25.1");var subQ2=sQuery(id+"F0.wireOp",EDGE,"E25.6");var subQ3=sQuery(id+"F0.wireOp",EDGE,"E25.5");var subQ4=sQuery(id+"F0.wireOp",EDGE,"E25.4");var subQ5=sQuery(id+"F0.wireOp",EDGE,"E25.0");var subQ6=sQuery(id+"F0.wireOp",EDGE,"E25.2");var subQ7=sQuery(id+"F0.wireOp",EDGE,"E25.3");Q4=makeQuery(id+"F8.boolean.opBoolean","INTERSECT",EDGE,{"derivedFrom":[makeQuery(id+"F5.boolean.opBoolean","SPLIT",FACE,{"disambiguationData":[TD([makeQuery(id+"F2.opExtrude","SWEPT_FACE",FACE,{"disambiguationData":[OSD([subQ5])]})])],"derivedFrom":makeQuery(id+"F3.boolean.opBoolean","COPY",FACE,{"derivedFrom":makeQuery(id+"F3.opExtrude","CAP_FACE",FACE,{"disambiguationData":[OSD([subQ5,subQ1,subQ6,subQ7,subQ4,subQ3,subQ2,subQ0])],"isStart":false})})}),makeQuery(id+"F8.opExtrude","SWEPT_FACE",FACE,{"disambiguationData":[OSD([sQuery(id+"F7.wireOp",EDGE,"E67")])]})]});}
            var Q5;
            Q5=makeQuery(id+"F8.boolean.opBoolean","INTERSECT",EDGE,{"disambiguationData":[OD(0.0)],"derivedFrom":[makeQuery(id+"F5.opExtrude","SWEPT_FACE",FACE,{"disambiguationData":[OSD([sQuery(id+"F4.wireOp",EDGE,"E30")])]}),makeQuery(id+"F8.opExtrude","SWEPT_FACE",FACE,{"disambiguationData":[OSD([sQuery(id+"F7.wireOp",EDGE,"E67")])]})]});
            fillet(context, id + "F14", {"entities" : qUnion([Q0, Q1, Q2, Q3, Q4, Q5]), "radius" : 3 * mm, "tangentPropagation" : true, "allowEdgeOverflow" : false});
        }
        {
            var Q0;
            Q0=makeQuery(id+"F1.opExtrude","CAP_EDGE",EDGE,{"disambiguationData":[OSD([sQuery(id+"F0.wireOp",EDGE,"E1.bottom")])],"isStart":false});
            fillet(context, id + "F15", {"entities" : qUnion([Q0]), "radius" : 2 * mm, "tangentPropagation" : true, "allowEdgeOverflow" : false});
        }
        {
            var Q0;
            {var subQ0=sQuery(id+"F0.wireOp",EDGE,"E21.filletArc");var subQ1=sQuery(id+"F0.wireOp",EDGE,"E7");var subQ2=sQuery(id+"F0.wireOp",EDGE,"E6");var subQ3=sQuery(id+"F0.wireOp",EDGE,"E5");var subQ4=sQuery(id+"F0.wireOp",EDGE,"E4");var subQ5=sQuery(id+"F0.wireOp",EDGE,"E22.filletArc");var subQ6=sQuery(id+"F0.wireOp",EDGE,"E1.bottom");var subQ7=sQuery(id+"F0.wireOp",EDGE,"E1.right");var subQ8=sQuery(id+"F0.wireOp",EDGE,"E1.top");var subQ9=sQuery(id+"F0.wireOp",EDGE,"E1.left");var subQ10=sQuery(id+"F0.wireOp",EDGE,"E23.filletArc");var subQ11=sQuery(id+"F0.wireOp",EDGE,"E24.filletArc");Q0=makeQuery(id+"F2.boolean.opBoolean","SPLIT",FACE,{"disambiguationData":[TD([makeQuery(id+"F1.opExtrude","SWEPT_FACE",FACE,{"disambiguationData":[OSD([subQ6])]})])],"derivedFrom":makeQuery(id+"F1.opExtrude","CAP_FACE",FACE,{"disambiguationData":[OSD([subQ6,subQ8,subQ9,subQ7,subQ4,subQ3,subQ2,subQ1,subQ0,subQ5,subQ10,subQ11])],"isStart":true})});}
            var sketch = newSketch(context, id + "F16", { "sketchPlane" : qUnion([Q0])});
            skLineSegment(sketch, "E79", {"start": v(0, 74.25) * mm, "end": v(0, 104.25) * mm, "construction": true});
            skArc(sketch, "E80", {"start": v(15, 104.25) * mm, "mid": v(0, 119.25) * mm, "end": v(-15, 104.25) * mm});
            skLineSegment(sketch, "E81", {"start": v(-15, 104.25) * mm, "end": v(-15, 90.11) * mm});
            skCircle(sketch, "E82", {"center": v(0, 104.25) * mm, "radius": 6 * mm});
            skLineSegment(sketch, "E83", {"start": v(15, 104.25) * mm, "end": v(15, 90.98) * mm});
            skLineSegment(sketch, "E84", {"start": v(15, 90.98) * mm, "end": v(31.73, 74.25) * mm});
            skLineSegment(sketch, "E85", {"start": v(-15, 90.11) * mm, "end": v(-30.86, 74.25) * mm});
            skLineSegment(sketch, "E86", {"start": v(-74.25, 0) * mm, "end": v(74.25, 0) * mm});
            skLineSegment(sketch, "E87.MirrorCS", {"start": v(15, -90.98) * mm, "end": v(31.73, -74.25) * mm});
            skLineSegment(sketch, "E88.MirrorCS", {"start": v(15, -104.25) * mm, "end": v(15, -90.98) * mm});
            skCircle(sketch, "E89.MirrorC", {"center": v(0, -104.25) * mm, "radius": 6 * mm});
            skLineSegment(sketch, "E90.MirrorCS", {"start": v(-15, -90.11) * mm, "end": v(-30.86, -74.25) * mm});
            skLineSegment(sketch, "E91.MirrorCS", {"start": v(0, -74.25) * mm, "end": v(0, -104.25) * mm, "construction": true});
            skLineSegment(sketch, "E92.MirrorCS", {"start": v(-15, -104.25) * mm, "end": v(-15, -90.11) * mm});
            skArc(sketch, "E93.MirrorCS", {"start": v(15, -104.25) * mm, "mid": v(0, -119.25) * mm, "end": v(-15, -104.25) * mm});
            skSolve(sketch);
        }
        {
            var Q0;
            Q0=makeQuery(id+"F16.imprint","IMPRINT",FACE,{"disambiguationData":[TD([[makeQuery(id+"F16.imprint","IMPRINT",EDGE,{"derivedFrom":sQuery(id+"F16.wireOp",EDGE,"E80")}),1.0]])]});
            var Q1;
            Q1=makeQuery(id+"F16.imprint","IMPRINT",FACE,{"disambiguationData":[TD([[makeQuery(id+"F16.imprint","IMPRINT",EDGE,{"derivedFrom":makeQuery(id+"F1.opExtrude","CAP_EDGE",EDGE,{"disambiguationData":[OSD([sQuery(id+"F0.wireOp",EDGE,"E4")])],"isStart":true})}),-1.0]])]});
            var Q2;
            Q2=makeQuery(id+"F16.imprint","IMPRINT",FACE,{"disambiguationData":[TD([[makeQuery(id+"F16.imprint","IMPRINT",EDGE,{"derivedFrom":makeQuery(id+"F1.opExtrude","CAP_EDGE",EDGE,{"disambiguationData":[OSD([sQuery(id+"F0.wireOp",EDGE,"E6")])],"isStart":true})}),-1.0]])]});
            var Q3;
            {var subQ1=sQuery(id+"F16.wireOp",EDGE,"E87.MirrorCS");Q3=makeQuery(id+"F16.imprint","IMPRINT",FACE,{"disambiguationData":[TD([[makeQuery(id+"F16.imprint","IMPRINT",EDGE,{"derivedFrom":subQ1}),1.0]])]});}
            extrude(context, id + "F17", {"entities" : qUnion([Q0, Q1, Q2, Q3]), "depth" : 5 * mm});
        }
    });
